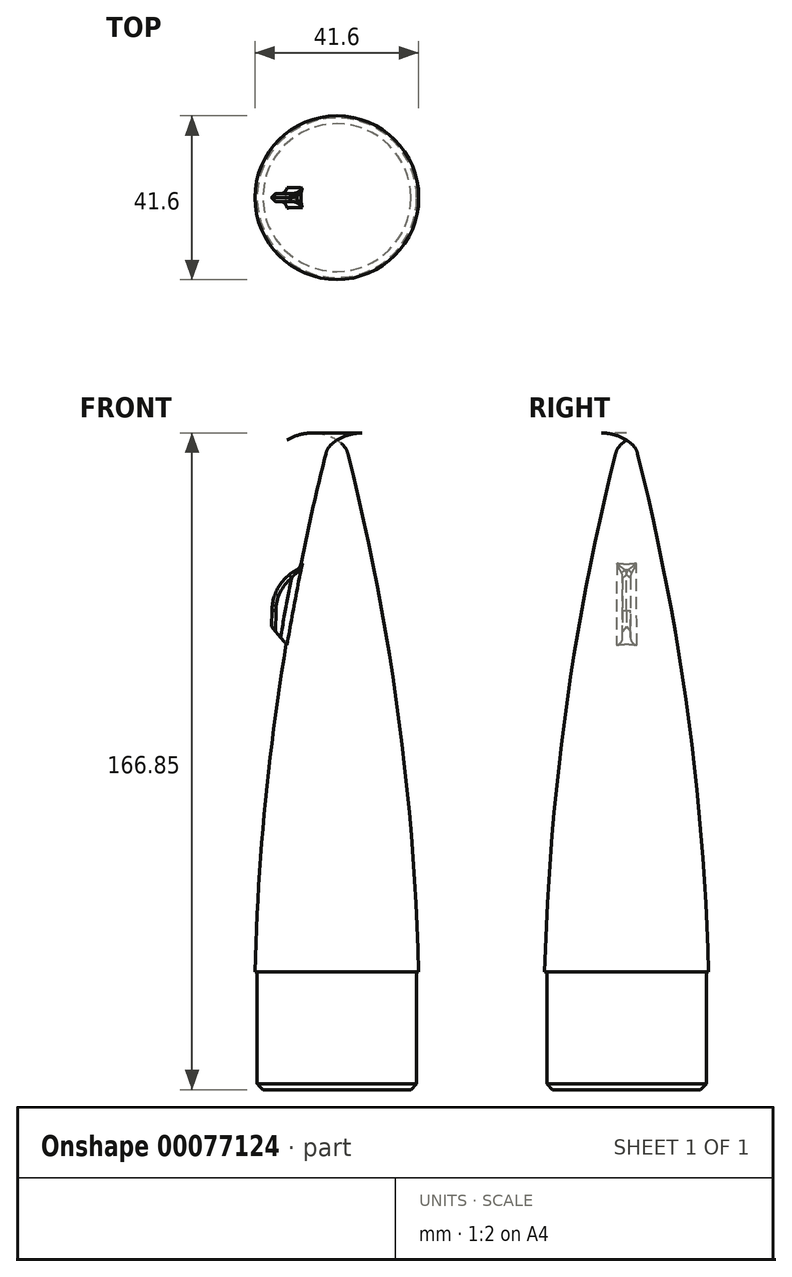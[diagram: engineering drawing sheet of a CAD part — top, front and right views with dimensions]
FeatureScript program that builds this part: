
annotation { "Feature Type Name" : "Feature", "Feature Type Description" : "" }
export const myFeature = defineFeature(function(context is Context, id is Id, definition is map)
    precondition{}
    {
        {
            var Q0;
            Q0=qCreatedBy(makeId("Front.planeOp"),FACE);
            var sketch = newSketch(context, id + "F0", { "sketchPlane" : qUnion([Q0])});
            skLineSegment(sketch, "E0", {"start": v(-20.8, -68.75) * mm, "end": v(-20.28, -68.75) * mm});
            skLineSegment(sketch, "E1", {"start": v(0, -68.75) * mm, "end": v(0, 86.96) * mm});
            skLineSegment(sketch, "E2", {"start": v(0, -68.75) * mm, "end": v(0, -98.75) * mm});
            skLineSegment(sketch, "E3", {"start": v(0, -98.75) * mm, "end": v(-20.28, -98.75) * mm});
            skLineSegment(sketch, "E4", {"start": v(-20.28, -98.75) * mm, "end": v(-20.28, -68.75) * mm});
            skLineSegment(sketch, "E5.trimOffspring", {"start": v(-20.28, -68.75) * mm, "end": v(-20.8, -68.75) * mm});
            skPoint(sketch, "E6.orphan", {"position": v(0, 71.25) * mm});
            skArc(sketch, "E7", {"start": v(0, 66.26) * mm, "mid": v(-1.3, 65.31) * mm, "end": v(-2.44, 64.2) * mm});
            skArc(sketch, "E8", {"start": v(-2.44, 64.2) * mm, "mid": v(-15.35, -1.76) * mm, "end": v(-20.8, -68.75) * mm});
            skPoint(sketch, "E8.second.point", {"position": v(1180, -68.75) * mm});
            skPoint(sketch, "E8.third.point", {"position": v(327.78, -629.15) * mm});
            skSolve(sketch);
        }
        {
            var Q0;
            Q0=makeQuery(id+"F0.imprint","IMPRINT",FACE,{"disambiguationData":[TD([[makeQuery(id+"F0.imprint","IMPRINT",EDGE,{"derivedFrom":sQuery(id+"F0.wireOp",EDGE,"Oh61cgLR-RQo2-T4aV-TcRg-Gp7ijPdUG9jl")}),1.0]])]});
            var Q1;
            {var subQ0=sQuery(id+"F0.wireOp",EDGE,"E2");Q1=makeQuery(id+"F0.imprint","IMPRINT",FACE,{"disambiguationData":[TD([[makeQuery(id+"F0.imprint","IMPRINT",EDGE,{"derivedFrom":subQ0}),-1.0]])]});}
            var Q2;
            Q2=sQuery(id+"F0.wireOp",EDGE,"E1");
            revolve(context, id + "F1", {"surfaceOperationType" : NewSurfaceOperationType.NEW, "entities" : qUnion([Q0, Q1]), "axis" : qUnion([Q2]), "revolveType" : RevolveType.FULL});
        }
        {
            var Q0;
            Q0=makeQuery(id+"F1.opRevolve","SWEPT_EDGE",EDGE,{"disambiguationData":[OSD([sQuery(id+"F0.wireOp",EDGE,"E3"),sQuery(id+"F0.wireOp",EDGE,"E4")])]});
            chamfer(context, id + "F2", {"entities" : qUnion([Q0]), "width" : 1.5 * mm, "tangentPropagation" : true});
        }
        {
            var Q0;
            Q0=qCreatedBy(makeId("Front.planeOp"),FACE);
            cPlane(context, id + "F3", {"entities" : qUnion([Q0]), "cplaneType" : CPlaneType.OFFSET, "offset" : 40 * mm, "width" : 150 * mm, "height" : 150 * mm});
        }
        {
            var Q0;
            Q0=qCreatedBy(id+"F3.planeOp",FACE);
            var sketch = newSketch(context, id + "F4", { "sketchPlane" : qUnion([Q0])});
            skText(sketch, "E9", { "text": "DC3Dparts", "fontName": "OpenSans-Regular.ttf"});
            const initialGuessF4  = {"E9": [-0.02787, -0.08817, 1, 0, 0.008]};
            skSetInitialGuess(sketch, initialGuessF4);
            skSolve(sketch);
        }
        {
            var Q0;
            Q0=qSketchRegion(id+"F4",true);
            var Q1;
            Q1=qCreatedBy(makeId("Front.planeOp"),FACE);
            extrude(context, id + "F5", {"entities" : qUnion([Q0]), "endBound" : BoundingType.UP_TO_SURFACE, "oppositeDirection" : true, "depth" : 25 * mm, "endBoundEntityFace" : qUnion([Q1]), "offsetDistance" : 25 * mm});
        }
        {
            var Q0;
            Q0=qCreatedBy(makeId("Front.planeOp"),FACE);
            var sketch = newSketch(context, id + "F6", { "sketchPlane" : qUnion([Q0])});
            skLineSegment(sketch, "E10.bottom", {"start": v(0, -71.45) * mm, "end": v(-32, -71.45) * mm});
            skLineSegment(sketch, "E10.top", {"start": v(0, -104.07) * mm, "end": v(-32, -104.07) * mm});
            skLineSegment(sketch, "E10.left", {"start": v(0, -71.45) * mm, "end": v(0, -104.07) * mm});
            skLineSegment(sketch, "E10.right", {"start": v(-32, -71.45) * mm, "end": v(-32, -104.07) * mm});
            skSolve(sketch);
        }
        {
            var Q0;
            Q0=makeQuery(id+"F6.imprint","IMPRINT",FACE,{"disambiguationData":[TD([[makeQuery(id+"F6.imprint","IMPRINT",EDGE,{"derivedFrom":sQuery(id+"F6.wireOp",EDGE,"E10.bottom")}),1.0]])]});
            var Q1;
            Q1=sQuery(id+"F6.wireOp",EDGE,"E10.left");
            revolve(context, id + "F7", {"entities" : qUnion([Q0]), "axis" : qUnion([Q1]), "revolveType" : RevolveType.FULL});
        }
        {
            var Q0;
            Q0=makeQuery(id+"F7.opRevolve","SWEPT_BODY",BODY,{"disambiguationData":[OSD([sQuery(id+"F6.wireOp",EDGE,"E10.bottom"),sQuery(id+"F6.wireOp",EDGE,"E10.top"),sQuery(id+"F6.wireOp",EDGE,"E10.left"),sQuery(id+"F6.wireOp",EDGE,"E10.right")])]});
            var Q1;
            Q1=makeQuery(id+"F5.opExtrude","SWEPT_BODY",BODY,{"disambiguationData":[OSD([sQuery(id+"F4.wireOp",EDGE,"E9.sketch_text.stroke-0"),sQuery(id+"F4.wireOp",EDGE,"E9.sketch_text.stroke-1"),sQuery(id+"F4.wireOp",EDGE,"E9.sketch_text.stroke-2"),sQuery(id+"F4.wireOp",EDGE,"E9.sketch_text.stroke-3"),sQuery(id+"F4.wireOp",EDGE,"E9.sketch_text.stroke-4"),sQuery(id+"F4.wireOp",EDGE,"E9.sketch_text.stroke-5"),sQuery(id+"F4.wireOp",EDGE,"E9.sketch_text.stroke-6"),sQuery(id+"F4.wireOp",EDGE,"E9.sketch_text.stroke-7"),sQuery(id+"F4.wireOp",EDGE,"E9.sketch_text.stroke-8"),sQuery(id+"F4.wireOp",EDGE,"E9.sketch_text.stroke-9"),sQuery(id+"F4.wireOp",EDGE,"E9.sketch_text.stroke-10"),sQuery(id+"F4.wireOp",EDGE,"E9.sketch_text.stroke-11"),sQuery(id+"F4.wireOp",EDGE,"E9.sketch_text.stroke-12"),sQuery(id+"F4.wireOp",EDGE,"E9.sketch_text.stroke-13")])]});
            var Q2;
            Q2=makeQuery(id+"F5.opExtrude","SWEPT_BODY",BODY,{"disambiguationData":[OSD([sQuery(id+"F4.wireOp",EDGE,"E9.sketch_text.stroke-14"),sQuery(id+"F4.wireOp",EDGE,"E9.sketch_text.stroke-15"),sQuery(id+"F4.wireOp",EDGE,"E9.sketch_text.stroke-16"),sQuery(id+"F4.wireOp",EDGE,"E9.sketch_text.stroke-17"),sQuery(id+"F4.wireOp",EDGE,"E9.sketch_text.stroke-18"),sQuery(id+"F4.wireOp",EDGE,"E9.sketch_text.stroke-19"),sQuery(id+"F4.wireOp",EDGE,"E9.sketch_text.stroke-20"),sQuery(id+"F4.wireOp",EDGE,"E9.sketch_text.stroke-21"),sQuery(id+"F4.wireOp",EDGE,"E9.sketch_text.stroke-22"),sQuery(id+"F4.wireOp",EDGE,"E9.sketch_text.stroke-23"),sQuery(id+"F4.wireOp",EDGE,"E9.sketch_text.stroke-24"),sQuery(id+"F4.wireOp",EDGE,"E9.sketch_text.stroke-25"),sQuery(id+"F4.wireOp",EDGE,"E9.sketch_text.stroke-26"),sQuery(id+"F4.wireOp",EDGE,"E9.sketch_text.stroke-27"),sQuery(id+"F4.wireOp",EDGE,"E9.sketch_text.stroke-28")])]});
            var Q3;
            Q3=makeQuery(id+"F5.opExtrude","SWEPT_BODY",BODY,{"disambiguationData":[OSD([sQuery(id+"F4.wireOp",EDGE,"E9.sketch_text.stroke-29"),sQuery(id+"F4.wireOp",EDGE,"E9.sketch_text.stroke-30"),sQuery(id+"F4.wireOp",EDGE,"E9.sketch_text.stroke-31"),sQuery(id+"F4.wireOp",EDGE,"E9.sketch_text.stroke-32"),sQuery(id+"F4.wireOp",EDGE,"E9.sketch_text.stroke-33"),sQuery(id+"F4.wireOp",EDGE,"E9.sketch_text.stroke-34"),sQuery(id+"F4.wireOp",EDGE,"E9.sketch_text.stroke-35"),sQuery(id+"F4.wireOp",EDGE,"E9.sketch_text.stroke-36"),sQuery(id+"F4.wireOp",EDGE,"E9.sketch_text.stroke-37"),sQuery(id+"F4.wireOp",EDGE,"E9.sketch_text.stroke-38"),sQuery(id+"F4.wireOp",EDGE,"E9.sketch_text.stroke-39"),sQuery(id+"F4.wireOp",EDGE,"E9.sketch_text.stroke-40"),sQuery(id+"F4.wireOp",EDGE,"E9.sketch_text.stroke-41"),sQuery(id+"F4.wireOp",EDGE,"E9.sketch_text.stroke-42"),sQuery(id+"F4.wireOp",EDGE,"E9.sketch_text.stroke-43"),sQuery(id+"F4.wireOp",EDGE,"E9.sketch_text.stroke-44"),sQuery(id+"F4.wireOp",EDGE,"E9.sketch_text.stroke-45"),sQuery(id+"F4.wireOp",EDGE,"E9.sketch_text.stroke-46"),sQuery(id+"F4.wireOp",EDGE,"E9.sketch_text.stroke-47"),sQuery(id+"F4.wireOp",EDGE,"E9.sketch_text.stroke-48"),sQuery(id+"F4.wireOp",EDGE,"E9.sketch_text.stroke-49"),sQuery(id+"F4.wireOp",EDGE,"E9.sketch_text.stroke-50"),sQuery(id+"F4.wireOp",EDGE,"E9.sketch_text.stroke-51"),sQuery(id+"F4.wireOp",EDGE,"E9.sketch_text.stroke-52"),sQuery(id+"F4.wireOp",EDGE,"E9.sketch_text.stroke-53"),sQuery(id+"F4.wireOp",EDGE,"E9.sketch_text.stroke-54"),sQuery(id+"F4.wireOp",EDGE,"E9.sketch_text.stroke-55"),sQuery(id+"F4.wireOp",EDGE,"E9.sketch_text.stroke-56")])]});
            var Q4;
            Q4=makeQuery(id+"F5.opExtrude","SWEPT_BODY",BODY,{"disambiguationData":[OSD([sQuery(id+"F4.wireOp",EDGE,"E9.sketch_text.stroke-57"),sQuery(id+"F4.wireOp",EDGE,"E9.sketch_text.stroke-58"),sQuery(id+"F4.wireOp",EDGE,"E9.sketch_text.stroke-59"),sQuery(id+"F4.wireOp",EDGE,"E9.sketch_text.stroke-60"),sQuery(id+"F4.wireOp",EDGE,"E9.sketch_text.stroke-61"),sQuery(id+"F4.wireOp",EDGE,"E9.sketch_text.stroke-62"),sQuery(id+"F4.wireOp",EDGE,"E9.sketch_text.stroke-63"),sQuery(id+"F4.wireOp",EDGE,"E9.sketch_text.stroke-64"),sQuery(id+"F4.wireOp",EDGE,"E9.sketch_text.stroke-65"),sQuery(id+"F4.wireOp",EDGE,"E9.sketch_text.stroke-66"),sQuery(id+"F4.wireOp",EDGE,"E9.sketch_text.stroke-67"),sQuery(id+"F4.wireOp",EDGE,"E9.sketch_text.stroke-68"),sQuery(id+"F4.wireOp",EDGE,"E9.sketch_text.stroke-69"),sQuery(id+"F4.wireOp",EDGE,"E9.sketch_text.stroke-70")])]});
            var Q5;
            Q5=makeQuery(id+"F5.opExtrude","SWEPT_BODY",BODY,{"disambiguationData":[OSD([sQuery(id+"F4.wireOp",EDGE,"E9.sketch_text.stroke-71"),sQuery(id+"F4.wireOp",EDGE,"E9.sketch_text.stroke-72"),sQuery(id+"F4.wireOp",EDGE,"E9.sketch_text.stroke-73"),sQuery(id+"F4.wireOp",EDGE,"E9.sketch_text.stroke-74"),sQuery(id+"F4.wireOp",EDGE,"E9.sketch_text.stroke-75"),sQuery(id+"F4.wireOp",EDGE,"E9.sketch_text.stroke-76"),sQuery(id+"F4.wireOp",EDGE,"E9.sketch_text.stroke-77"),sQuery(id+"F4.wireOp",EDGE,"E9.sketch_text.stroke-78"),sQuery(id+"F4.wireOp",EDGE,"E9.sketch_text.stroke-79"),sQuery(id+"F4.wireOp",EDGE,"E9.sketch_text.stroke-80"),sQuery(id+"F4.wireOp",EDGE,"E9.sketch_text.stroke-81"),sQuery(id+"F4.wireOp",EDGE,"E9.sketch_text.stroke-82"),sQuery(id+"F4.wireOp",EDGE,"E9.sketch_text.stroke-83"),sQuery(id+"F4.wireOp",EDGE,"E9.sketch_text.stroke-84"),sQuery(id+"F4.wireOp",EDGE,"E9.sketch_text.stroke-85"),sQuery(id+"F4.wireOp",EDGE,"E9.sketch_text.stroke-86"),sQuery(id+"F4.wireOp",EDGE,"E9.sketch_text.stroke-87"),sQuery(id+"F4.wireOp",EDGE,"E9.sketch_text.stroke-88"),sQuery(id+"F4.wireOp",EDGE,"E9.sketch_text.stroke-89"),sQuery(id+"F4.wireOp",EDGE,"E9.sketch_text.stroke-90"),sQuery(id+"F4.wireOp",EDGE,"E9.sketch_text.stroke-91"),sQuery(id+"F4.wireOp",EDGE,"E9.sketch_text.stroke-92"),sQuery(id+"F4.wireOp",EDGE,"E9.sketch_text.stroke-93"),sQuery(id+"F4.wireOp",EDGE,"E9.sketch_text.stroke-94"),sQuery(id+"F4.wireOp",EDGE,"E9.sketch_text.stroke-95")])]});
            var Q6;
            Q6=makeQuery(id+"F5.opExtrude","SWEPT_BODY",BODY,{"disambiguationData":[OSD([sQuery(id+"F4.wireOp",EDGE,"E9.sketch_text.stroke-136"),sQuery(id+"F4.wireOp",EDGE,"E9.sketch_text.stroke-137"),sQuery(id+"F4.wireOp",EDGE,"E9.sketch_text.stroke-138"),sQuery(id+"F4.wireOp",EDGE,"E9.sketch_text.stroke-139"),sQuery(id+"F4.wireOp",EDGE,"E9.sketch_text.stroke-140"),sQuery(id+"F4.wireOp",EDGE,"E9.sketch_text.stroke-141"),sQuery(id+"F4.wireOp",EDGE,"E9.sketch_text.stroke-142"),sQuery(id+"F4.wireOp",EDGE,"E9.sketch_text.stroke-143"),sQuery(id+"F4.wireOp",EDGE,"E9.sketch_text.stroke-144"),sQuery(id+"F4.wireOp",EDGE,"E9.sketch_text.stroke-145"),sQuery(id+"F4.wireOp",EDGE,"E9.sketch_text.stroke-146"),sQuery(id+"F4.wireOp",EDGE,"E9.sketch_text.stroke-147"),sQuery(id+"F4.wireOp",EDGE,"E9.sketch_text.stroke-148"),sQuery(id+"F4.wireOp",EDGE,"E9.sketch_text.stroke-149"),sQuery(id+"F4.wireOp",EDGE,"E9.sketch_text.stroke-150"),sQuery(id+"F4.wireOp",EDGE,"E9.sketch_text.stroke-151"),sQuery(id+"F4.wireOp",EDGE,"E9.sketch_text.stroke-152"),sQuery(id+"F4.wireOp",EDGE,"E9.sketch_text.stroke-153"),sQuery(id+"F4.wireOp",EDGE,"E9.sketch_text.stroke-154")])]});
            var Q7;
            Q7=makeQuery(id+"F5.opExtrude","SWEPT_BODY",BODY,{"disambiguationData":[OSD([sQuery(id+"F4.wireOp",EDGE,"E9.sketch_text.stroke-155"),sQuery(id+"F4.wireOp",EDGE,"E9.sketch_text.stroke-156"),sQuery(id+"F4.wireOp",EDGE,"E9.sketch_text.stroke-157"),sQuery(id+"F4.wireOp",EDGE,"E9.sketch_text.stroke-158"),sQuery(id+"F4.wireOp",EDGE,"E9.sketch_text.stroke-159"),sQuery(id+"F4.wireOp",EDGE,"E9.sketch_text.stroke-160"),sQuery(id+"F4.wireOp",EDGE,"E9.sketch_text.stroke-161"),sQuery(id+"F4.wireOp",EDGE,"E9.sketch_text.stroke-162"),sQuery(id+"F4.wireOp",EDGE,"E9.sketch_text.stroke-163"),sQuery(id+"F4.wireOp",EDGE,"E9.sketch_text.stroke-164"),sQuery(id+"F4.wireOp",EDGE,"E9.sketch_text.stroke-165"),sQuery(id+"F4.wireOp",EDGE,"E9.sketch_text.stroke-166"),sQuery(id+"F4.wireOp",EDGE,"E9.sketch_text.stroke-167"),sQuery(id+"F4.wireOp",EDGE,"E9.sketch_text.stroke-168"),sQuery(id+"F4.wireOp",EDGE,"E9.sketch_text.stroke-169"),sQuery(id+"F4.wireOp",EDGE,"E9.sketch_text.stroke-170"),sQuery(id+"F4.wireOp",EDGE,"E9.sketch_text.stroke-171"),sQuery(id+"F4.wireOp",EDGE,"E9.sketch_text.stroke-172"),sQuery(id+"F4.wireOp",EDGE,"E9.sketch_text.stroke-173"),sQuery(id+"F4.wireOp",EDGE,"E9.sketch_text.stroke-174"),sQuery(id+"F4.wireOp",EDGE,"E9.sketch_text.stroke-175"),sQuery(id+"F4.wireOp",EDGE,"E9.sketch_text.stroke-176"),sQuery(id+"F4.wireOp",EDGE,"E9.sketch_text.stroke-177"),sQuery(id+"F4.wireOp",EDGE,"E9.sketch_text.stroke-178"),sQuery(id+"F4.wireOp",EDGE,"E9.sketch_text.stroke-179")])]});
            var Q8;
            Q8=makeQuery(id+"F5.opExtrude","SWEPT_BODY",BODY,{"disambiguationData":[OSD([sQuery(id+"F4.wireOp",EDGE,"E9.sketch_text.stroke-96"),sQuery(id+"F4.wireOp",EDGE,"E9.sketch_text.stroke-97"),sQuery(id+"F4.wireOp",EDGE,"E9.sketch_text.stroke-98"),sQuery(id+"F4.wireOp",EDGE,"E9.sketch_text.stroke-99"),sQuery(id+"F4.wireOp",EDGE,"E9.sketch_text.stroke-100"),sQuery(id+"F4.wireOp",EDGE,"E9.sketch_text.stroke-101"),sQuery(id+"F4.wireOp",EDGE,"E9.sketch_text.stroke-102"),sQuery(id+"F4.wireOp",EDGE,"E9.sketch_text.stroke-103"),sQuery(id+"F4.wireOp",EDGE,"E9.sketch_text.stroke-104"),sQuery(id+"F4.wireOp",EDGE,"E9.sketch_text.stroke-105"),sQuery(id+"F4.wireOp",EDGE,"E9.sketch_text.stroke-106"),sQuery(id+"F4.wireOp",EDGE,"E9.sketch_text.stroke-107"),sQuery(id+"F4.wireOp",EDGE,"E9.sketch_text.stroke-108"),sQuery(id+"F4.wireOp",EDGE,"E9.sketch_text.stroke-109"),sQuery(id+"F4.wireOp",EDGE,"E9.sketch_text.stroke-110"),sQuery(id+"F4.wireOp",EDGE,"E9.sketch_text.stroke-111"),sQuery(id+"F4.wireOp",EDGE,"E9.sketch_text.stroke-112"),sQuery(id+"F4.wireOp",EDGE,"E9.sketch_text.stroke-113"),sQuery(id+"F4.wireOp",EDGE,"E9.sketch_text.stroke-114"),sQuery(id+"F4.wireOp",EDGE,"E9.sketch_text.stroke-115"),sQuery(id+"F4.wireOp",EDGE,"E9.sketch_text.stroke-116"),sQuery(id+"F4.wireOp",EDGE,"E9.sketch_text.stroke-117"),sQuery(id+"F4.wireOp",EDGE,"E9.sketch_text.stroke-118"),sQuery(id+"F4.wireOp",EDGE,"E9.sketch_text.stroke-119"),sQuery(id+"F4.wireOp",EDGE,"E9.sketch_text.stroke-120"),sQuery(id+"F4.wireOp",EDGE,"E9.sketch_text.stroke-121"),sQuery(id+"F4.wireOp",EDGE,"E9.sketch_text.stroke-122")])]});
            var Q9;
            Q9=makeQuery(id+"F5.opExtrude","SWEPT_BODY",BODY,{"disambiguationData":[OSD([sQuery(id+"F4.wireOp",EDGE,"E9.sketch_text.stroke-123"),sQuery(id+"F4.wireOp",EDGE,"E9.sketch_text.stroke-124"),sQuery(id+"F4.wireOp",EDGE,"E9.sketch_text.stroke-125"),sQuery(id+"F4.wireOp",EDGE,"E9.sketch_text.stroke-126"),sQuery(id+"F4.wireOp",EDGE,"E9.sketch_text.stroke-127"),sQuery(id+"F4.wireOp",EDGE,"E9.sketch_text.stroke-128"),sQuery(id+"F4.wireOp",EDGE,"E9.sketch_text.stroke-129"),sQuery(id+"F4.wireOp",EDGE,"E9.sketch_text.stroke-130"),sQuery(id+"F4.wireOp",EDGE,"E9.sketch_text.stroke-131"),sQuery(id+"F4.wireOp",EDGE,"E9.sketch_text.stroke-132"),sQuery(id+"F4.wireOp",EDGE,"E9.sketch_text.stroke-133"),sQuery(id+"F4.wireOp",EDGE,"E9.sketch_text.stroke-134"),sQuery(id+"F4.wireOp",EDGE,"E9.sketch_text.stroke-135")])]});
            booleanBodies(context, id + "F8", {"operationType" : BooleanOperationType.SUBTRACTION, "tools" : qUnion([Q0]), "targets" : qUnion([Q1, Q2, Q3, Q4, Q5, Q6, Q7, Q8, Q9])});
        }
        {
            var Q0;
            Q0=makeQuery(id+"F5.opExtrude","SWEPT_BODY",BODY,{"disambiguationData":[OSD([sQuery(id+"F4.wireOp",EDGE,"E9.sketch_text.stroke-0"),sQuery(id+"F4.wireOp",EDGE,"E9.sketch_text.stroke-1"),sQuery(id+"F4.wireOp",EDGE,"E9.sketch_text.stroke-2"),sQuery(id+"F4.wireOp",EDGE,"E9.sketch_text.stroke-3"),sQuery(id+"F4.wireOp",EDGE,"E9.sketch_text.stroke-4"),sQuery(id+"F4.wireOp",EDGE,"E9.sketch_text.stroke-5"),sQuery(id+"F4.wireOp",EDGE,"E9.sketch_text.stroke-6"),sQuery(id+"F4.wireOp",EDGE,"E9.sketch_text.stroke-7"),sQuery(id+"F4.wireOp",EDGE,"E9.sketch_text.stroke-8"),sQuery(id+"F4.wireOp",EDGE,"E9.sketch_text.stroke-9"),sQuery(id+"F4.wireOp",EDGE,"E9.sketch_text.stroke-10"),sQuery(id+"F4.wireOp",EDGE,"E9.sketch_text.stroke-11"),sQuery(id+"F4.wireOp",EDGE,"E9.sketch_text.stroke-12"),sQuery(id+"F4.wireOp",EDGE,"E9.sketch_text.stroke-13")])]});
            var Q1;
            Q1=makeQuery(id+"F5.opExtrude","SWEPT_BODY",BODY,{"disambiguationData":[OSD([sQuery(id+"F4.wireOp",EDGE,"E9.sketch_text.stroke-14"),sQuery(id+"F4.wireOp",EDGE,"E9.sketch_text.stroke-15"),sQuery(id+"F4.wireOp",EDGE,"E9.sketch_text.stroke-16"),sQuery(id+"F4.wireOp",EDGE,"E9.sketch_text.stroke-17"),sQuery(id+"F4.wireOp",EDGE,"E9.sketch_text.stroke-18"),sQuery(id+"F4.wireOp",EDGE,"E9.sketch_text.stroke-19"),sQuery(id+"F4.wireOp",EDGE,"E9.sketch_text.stroke-20"),sQuery(id+"F4.wireOp",EDGE,"E9.sketch_text.stroke-21"),sQuery(id+"F4.wireOp",EDGE,"E9.sketch_text.stroke-22"),sQuery(id+"F4.wireOp",EDGE,"E9.sketch_text.stroke-23"),sQuery(id+"F4.wireOp",EDGE,"E9.sketch_text.stroke-24"),sQuery(id+"F4.wireOp",EDGE,"E9.sketch_text.stroke-25"),sQuery(id+"F4.wireOp",EDGE,"E9.sketch_text.stroke-26"),sQuery(id+"F4.wireOp",EDGE,"E9.sketch_text.stroke-27"),sQuery(id+"F4.wireOp",EDGE,"E9.sketch_text.stroke-28")])]});
            var Q2;
            Q2=makeQuery(id+"F5.opExtrude","SWEPT_BODY",BODY,{"disambiguationData":[OSD([sQuery(id+"F4.wireOp",EDGE,"E9.sketch_text.stroke-29"),sQuery(id+"F4.wireOp",EDGE,"E9.sketch_text.stroke-30"),sQuery(id+"F4.wireOp",EDGE,"E9.sketch_text.stroke-31"),sQuery(id+"F4.wireOp",EDGE,"E9.sketch_text.stroke-32"),sQuery(id+"F4.wireOp",EDGE,"E9.sketch_text.stroke-33"),sQuery(id+"F4.wireOp",EDGE,"E9.sketch_text.stroke-34"),sQuery(id+"F4.wireOp",EDGE,"E9.sketch_text.stroke-35"),sQuery(id+"F4.wireOp",EDGE,"E9.sketch_text.stroke-36"),sQuery(id+"F4.wireOp",EDGE,"E9.sketch_text.stroke-37"),sQuery(id+"F4.wireOp",EDGE,"E9.sketch_text.stroke-38"),sQuery(id+"F4.wireOp",EDGE,"E9.sketch_text.stroke-39"),sQuery(id+"F4.wireOp",EDGE,"E9.sketch_text.stroke-40"),sQuery(id+"F4.wireOp",EDGE,"E9.sketch_text.stroke-41"),sQuery(id+"F4.wireOp",EDGE,"E9.sketch_text.stroke-42"),sQuery(id+"F4.wireOp",EDGE,"E9.sketch_text.stroke-43"),sQuery(id+"F4.wireOp",EDGE,"E9.sketch_text.stroke-44"),sQuery(id+"F4.wireOp",EDGE,"E9.sketch_text.stroke-45"),sQuery(id+"F4.wireOp",EDGE,"E9.sketch_text.stroke-46"),sQuery(id+"F4.wireOp",EDGE,"E9.sketch_text.stroke-47"),sQuery(id+"F4.wireOp",EDGE,"E9.sketch_text.stroke-48"),sQuery(id+"F4.wireOp",EDGE,"E9.sketch_text.stroke-49"),sQuery(id+"F4.wireOp",EDGE,"E9.sketch_text.stroke-50"),sQuery(id+"F4.wireOp",EDGE,"E9.sketch_text.stroke-51"),sQuery(id+"F4.wireOp",EDGE,"E9.sketch_text.stroke-52"),sQuery(id+"F4.wireOp",EDGE,"E9.sketch_text.stroke-53"),sQuery(id+"F4.wireOp",EDGE,"E9.sketch_text.stroke-54"),sQuery(id+"F4.wireOp",EDGE,"E9.sketch_text.stroke-55"),sQuery(id+"F4.wireOp",EDGE,"E9.sketch_text.stroke-56")])]});
            var Q3;
            Q3=makeQuery(id+"F5.opExtrude","SWEPT_BODY",BODY,{"disambiguationData":[OSD([sQuery(id+"F4.wireOp",EDGE,"E9.sketch_text.stroke-57"),sQuery(id+"F4.wireOp",EDGE,"E9.sketch_text.stroke-58"),sQuery(id+"F4.wireOp",EDGE,"E9.sketch_text.stroke-59"),sQuery(id+"F4.wireOp",EDGE,"E9.sketch_text.stroke-60"),sQuery(id+"F4.wireOp",EDGE,"E9.sketch_text.stroke-61"),sQuery(id+"F4.wireOp",EDGE,"E9.sketch_text.stroke-62"),sQuery(id+"F4.wireOp",EDGE,"E9.sketch_text.stroke-63"),sQuery(id+"F4.wireOp",EDGE,"E9.sketch_text.stroke-64"),sQuery(id+"F4.wireOp",EDGE,"E9.sketch_text.stroke-65"),sQuery(id+"F4.wireOp",EDGE,"E9.sketch_text.stroke-66"),sQuery(id+"F4.wireOp",EDGE,"E9.sketch_text.stroke-67"),sQuery(id+"F4.wireOp",EDGE,"E9.sketch_text.stroke-68"),sQuery(id+"F4.wireOp",EDGE,"E9.sketch_text.stroke-69"),sQuery(id+"F4.wireOp",EDGE,"E9.sketch_text.stroke-70")])]});
            var Q4;
            Q4=makeQuery(id+"F5.opExtrude","SWEPT_BODY",BODY,{"disambiguationData":[OSD([sQuery(id+"F4.wireOp",EDGE,"E9.sketch_text.stroke-71"),sQuery(id+"F4.wireOp",EDGE,"E9.sketch_text.stroke-72"),sQuery(id+"F4.wireOp",EDGE,"E9.sketch_text.stroke-73"),sQuery(id+"F4.wireOp",EDGE,"E9.sketch_text.stroke-74"),sQuery(id+"F4.wireOp",EDGE,"E9.sketch_text.stroke-75"),sQuery(id+"F4.wireOp",EDGE,"E9.sketch_text.stroke-76"),sQuery(id+"F4.wireOp",EDGE,"E9.sketch_text.stroke-77"),sQuery(id+"F4.wireOp",EDGE,"E9.sketch_text.stroke-78"),sQuery(id+"F4.wireOp",EDGE,"E9.sketch_text.stroke-79"),sQuery(id+"F4.wireOp",EDGE,"E9.sketch_text.stroke-80"),sQuery(id+"F4.wireOp",EDGE,"E9.sketch_text.stroke-81"),sQuery(id+"F4.wireOp",EDGE,"E9.sketch_text.stroke-82"),sQuery(id+"F4.wireOp",EDGE,"E9.sketch_text.stroke-83"),sQuery(id+"F4.wireOp",EDGE,"E9.sketch_text.stroke-84"),sQuery(id+"F4.wireOp",EDGE,"E9.sketch_text.stroke-85"),sQuery(id+"F4.wireOp",EDGE,"E9.sketch_text.stroke-86"),sQuery(id+"F4.wireOp",EDGE,"E9.sketch_text.stroke-87"),sQuery(id+"F4.wireOp",EDGE,"E9.sketch_text.stroke-88"),sQuery(id+"F4.wireOp",EDGE,"E9.sketch_text.stroke-89"),sQuery(id+"F4.wireOp",EDGE,"E9.sketch_text.stroke-90"),sQuery(id+"F4.wireOp",EDGE,"E9.sketch_text.stroke-91"),sQuery(id+"F4.wireOp",EDGE,"E9.sketch_text.stroke-92"),sQuery(id+"F4.wireOp",EDGE,"E9.sketch_text.stroke-93"),sQuery(id+"F4.wireOp",EDGE,"E9.sketch_text.stroke-94"),sQuery(id+"F4.wireOp",EDGE,"E9.sketch_text.stroke-95")])]});
            var Q5;
            Q5=makeQuery(id+"F5.opExtrude","SWEPT_BODY",BODY,{"disambiguationData":[OSD([sQuery(id+"F4.wireOp",EDGE,"E9.sketch_text.stroke-96"),sQuery(id+"F4.wireOp",EDGE,"E9.sketch_text.stroke-97"),sQuery(id+"F4.wireOp",EDGE,"E9.sketch_text.stroke-98"),sQuery(id+"F4.wireOp",EDGE,"E9.sketch_text.stroke-99"),sQuery(id+"F4.wireOp",EDGE,"E9.sketch_text.stroke-100"),sQuery(id+"F4.wireOp",EDGE,"E9.sketch_text.stroke-101"),sQuery(id+"F4.wireOp",EDGE,"E9.sketch_text.stroke-102"),sQuery(id+"F4.wireOp",EDGE,"E9.sketch_text.stroke-103"),sQuery(id+"F4.wireOp",EDGE,"E9.sketch_text.stroke-104"),sQuery(id+"F4.wireOp",EDGE,"E9.sketch_text.stroke-105"),sQuery(id+"F4.wireOp",EDGE,"E9.sketch_text.stroke-106"),sQuery(id+"F4.wireOp",EDGE,"E9.sketch_text.stroke-107"),sQuery(id+"F4.wireOp",EDGE,"E9.sketch_text.stroke-108"),sQuery(id+"F4.wireOp",EDGE,"E9.sketch_text.stroke-109"),sQuery(id+"F4.wireOp",EDGE,"E9.sketch_text.stroke-110"),sQuery(id+"F4.wireOp",EDGE,"E9.sketch_text.stroke-111"),sQuery(id+"F4.wireOp",EDGE,"E9.sketch_text.stroke-112"),sQuery(id+"F4.wireOp",EDGE,"E9.sketch_text.stroke-113"),sQuery(id+"F4.wireOp",EDGE,"E9.sketch_text.stroke-114"),sQuery(id+"F4.wireOp",EDGE,"E9.sketch_text.stroke-115"),sQuery(id+"F4.wireOp",EDGE,"E9.sketch_text.stroke-116"),sQuery(id+"F4.wireOp",EDGE,"E9.sketch_text.stroke-117"),sQuery(id+"F4.wireOp",EDGE,"E9.sketch_text.stroke-118"),sQuery(id+"F4.wireOp",EDGE,"E9.sketch_text.stroke-119"),sQuery(id+"F4.wireOp",EDGE,"E9.sketch_text.stroke-120"),sQuery(id+"F4.wireOp",EDGE,"E9.sketch_text.stroke-121"),sQuery(id+"F4.wireOp",EDGE,"E9.sketch_text.stroke-122")])]});
            var Q6;
            Q6=makeQuery(id+"F5.opExtrude","SWEPT_BODY",BODY,{"disambiguationData":[OSD([sQuery(id+"F4.wireOp",EDGE,"E9.sketch_text.stroke-123"),sQuery(id+"F4.wireOp",EDGE,"E9.sketch_text.stroke-124"),sQuery(id+"F4.wireOp",EDGE,"E9.sketch_text.stroke-125"),sQuery(id+"F4.wireOp",EDGE,"E9.sketch_text.stroke-126"),sQuery(id+"F4.wireOp",EDGE,"E9.sketch_text.stroke-127"),sQuery(id+"F4.wireOp",EDGE,"E9.sketch_text.stroke-128"),sQuery(id+"F4.wireOp",EDGE,"E9.sketch_text.stroke-129"),sQuery(id+"F4.wireOp",EDGE,"E9.sketch_text.stroke-130"),sQuery(id+"F4.wireOp",EDGE,"E9.sketch_text.stroke-131"),sQuery(id+"F4.wireOp",EDGE,"E9.sketch_text.stroke-132"),sQuery(id+"F4.wireOp",EDGE,"E9.sketch_text.stroke-133"),sQuery(id+"F4.wireOp",EDGE,"E9.sketch_text.stroke-134"),sQuery(id+"F4.wireOp",EDGE,"E9.sketch_text.stroke-135")])]});
            var Q7;
            Q7=makeQuery(id+"F5.opExtrude","SWEPT_BODY",BODY,{"disambiguationData":[OSD([sQuery(id+"F4.wireOp",EDGE,"E9.sketch_text.stroke-155"),sQuery(id+"F4.wireOp",EDGE,"E9.sketch_text.stroke-156"),sQuery(id+"F4.wireOp",EDGE,"E9.sketch_text.stroke-157"),sQuery(id+"F4.wireOp",EDGE,"E9.sketch_text.stroke-158"),sQuery(id+"F4.wireOp",EDGE,"E9.sketch_text.stroke-159"),sQuery(id+"F4.wireOp",EDGE,"E9.sketch_text.stroke-160"),sQuery(id+"F4.wireOp",EDGE,"E9.sketch_text.stroke-161"),sQuery(id+"F4.wireOp",EDGE,"E9.sketch_text.stroke-162"),sQuery(id+"F4.wireOp",EDGE,"E9.sketch_text.stroke-163"),sQuery(id+"F4.wireOp",EDGE,"E9.sketch_text.stroke-164"),sQuery(id+"F4.wireOp",EDGE,"E9.sketch_text.stroke-165"),sQuery(id+"F4.wireOp",EDGE,"E9.sketch_text.stroke-166"),sQuery(id+"F4.wireOp",EDGE,"E9.sketch_text.stroke-167"),sQuery(id+"F4.wireOp",EDGE,"E9.sketch_text.stroke-168"),sQuery(id+"F4.wireOp",EDGE,"E9.sketch_text.stroke-169"),sQuery(id+"F4.wireOp",EDGE,"E9.sketch_text.stroke-170"),sQuery(id+"F4.wireOp",EDGE,"E9.sketch_text.stroke-171"),sQuery(id+"F4.wireOp",EDGE,"E9.sketch_text.stroke-172"),sQuery(id+"F4.wireOp",EDGE,"E9.sketch_text.stroke-173"),sQuery(id+"F4.wireOp",EDGE,"E9.sketch_text.stroke-174"),sQuery(id+"F4.wireOp",EDGE,"E9.sketch_text.stroke-175"),sQuery(id+"F4.wireOp",EDGE,"E9.sketch_text.stroke-176"),sQuery(id+"F4.wireOp",EDGE,"E9.sketch_text.stroke-177"),sQuery(id+"F4.wireOp",EDGE,"E9.sketch_text.stroke-178"),sQuery(id+"F4.wireOp",EDGE,"E9.sketch_text.stroke-179")])]});
            var Q8;
            Q8=makeQuery(id+"F5.opExtrude","SWEPT_BODY",BODY,{"disambiguationData":[OSD([sQuery(id+"F4.wireOp",EDGE,"E9.sketch_text.stroke-136"),sQuery(id+"F4.wireOp",EDGE,"E9.sketch_text.stroke-137"),sQuery(id+"F4.wireOp",EDGE,"E9.sketch_text.stroke-138"),sQuery(id+"F4.wireOp",EDGE,"E9.sketch_text.stroke-139"),sQuery(id+"F4.wireOp",EDGE,"E9.sketch_text.stroke-140"),sQuery(id+"F4.wireOp",EDGE,"E9.sketch_text.stroke-141"),sQuery(id+"F4.wireOp",EDGE,"E9.sketch_text.stroke-142"),sQuery(id+"F4.wireOp",EDGE,"E9.sketch_text.stroke-143"),sQuery(id+"F4.wireOp",EDGE,"E9.sketch_text.stroke-144"),sQuery(id+"F4.wireOp",EDGE,"E9.sketch_text.stroke-145"),sQuery(id+"F4.wireOp",EDGE,"E9.sketch_text.stroke-146"),sQuery(id+"F4.wireOp",EDGE,"E9.sketch_text.stroke-147"),sQuery(id+"F4.wireOp",EDGE,"E9.sketch_text.stroke-148"),sQuery(id+"F4.wireOp",EDGE,"E9.sketch_text.stroke-149"),sQuery(id+"F4.wireOp",EDGE,"E9.sketch_text.stroke-150"),sQuery(id+"F4.wireOp",EDGE,"E9.sketch_text.stroke-151"),sQuery(id+"F4.wireOp",EDGE,"E9.sketch_text.stroke-152"),sQuery(id+"F4.wireOp",EDGE,"E9.sketch_text.stroke-153"),sQuery(id+"F4.wireOp",EDGE,"E9.sketch_text.stroke-154")])]});
            var Q9;
            Q9=makeQuery(id+"F1.opRevolve","SWEPT_BODY",BODY,{"disambiguationData":[OSD([sQuery(id+"F0.wireOp",EDGE,"Oh61cgLR-RQo2-T4aV-TcRg-Gp7ijPdUG9jl"),sQuery(id+"F0.wireOp",EDGE,"E1"),sQuery(id+"F0.wireOp",EDGE,"E2"),sQuery(id+"F0.wireOp",EDGE,"E3"),sQuery(id+"F0.wireOp",EDGE,"E4"),sQuery(id+"F0.wireOp",EDGE,"E5.trimOffspring"),sQuery(id+"F0.wireOp",EDGE,"dTV1AxgJ-VMAe-DLQO-Zqz3-4UbtDb8FiUJC")])]});
            booleanBodies(context, id + "F9", {"operationType" : BooleanOperationType.SUBTRACTION, "tools" : qUnion([Q0, Q1, Q2, Q3, Q4, Q5, Q6, Q7, Q8]), "targets" : qUnion([Q9])});
        }
        {
            var Q0;
            Q0=makeQuery(id+"F1.opRevolve","SWEPT_EDGE",EDGE,{"disambiguationData":[OSD([sQuery(id+"F0.wireOp",EDGE,"E7"),sQuery(id+"F0.wireOp",EDGE,"E8")])]});
            fillet(context, id + "F10", {"entities" : qUnion([Q0]), "radius" : 5 * mm, "tangentPropagation" : true, "allowEdgeOverflow" : false});
        }
        {
            var Q0;
            Q0=qCreatedBy(makeId("Front.planeOp"),FACE);
            var sketch = newSketch(context, id + "F11", { "sketchPlane" : qUnion([Q0])});
            skArc(sketch, "E11", {"start": v(-8.7, 34.02) * mm, "mid": v(-14.33, 29.71) * mm, "end": v(-16.5, 22.97) * mm});
            skLineSegment(sketch, "E12", {"start": v(-8.7, 34.02) * mm, "end": v(-12.38, 13.85) * mm});
            skArc(sketch, "E13.MirrorCS", {"start": v(8.7, 34.02) * mm, "mid": v(14.33, 29.71) * mm, "end": v(16.5, 22.97) * mm});
            skLineSegment(sketch, "E14.MirrorCS", {"start": v(8.7, 34.02) * mm, "end": v(12.38, 13.85) * mm});
            skLineSegment(sketch, "E15", {"start": v(-12.38, 13.85) * mm, "end": v(-16.6, 18.9) * mm});
            skLineSegment(sketch, "E16", {"start": v(-16.6, 18.9) * mm, "end": v(-16.5, 22.97) * mm});
            skLineSegment(sketch, "E17.MirrorCS", {"start": v(12.38, 13.85) * mm, "end": v(16.6, 18.9) * mm});
            skLineSegment(sketch, "E18.MirrorCS", {"start": v(16.6, 18.9) * mm, "end": v(16.5, 22.97) * mm});
            skPoint(sketch, "E19.orphan", {"position": v(12.38, 13.85) * mm});
            skSolve(sketch);
        }
        {
            var Q0;
            Q0=makeQuery(id+"F11.imprint","IMPRINT",FACE,{"disambiguationData":[TD([[makeQuery(id+"F11.imprint","IMPRINT",EDGE,{"derivedFrom":sQuery(id+"F11.wireOp",EDGE,"E11")}),1.0]])]});
            var Q1;
            Q1=makeQuery(id+"F11.imprint","IMPRINT",FACE,{"disambiguationData":[TD([[makeQuery(id+"F11.imprint","IMPRINT",EDGE,{"derivedFrom":sQuery(id+"F11.wireOp",EDGE,"E13.MirrorCS")}),-1.0]])]});
            extrude(context, id + "F12", {"entities" : qUnion([Q0, Q1]), "operationType" : NewBodyOperationType.ADD, "depth" : 2 * mm, "offsetDistance" : 25 * mm, "symmetric" : true});
        }
        {
            var Q0;
            Q0=makeQuery(id+"F12.boolean.opBoolean","INTERSECT",EDGE,{"derivedFrom":[makeQuery(id+"F1.opRevolve","SWEPT_FACE",FACE,{"disambiguationData":[OSD([sQuery(id+"F0.wireOp",EDGE,"E8")])]}),makeQuery(id+"F12.opExtrude","CAP_FACE",FACE,{"disambiguationData":[OSD([sQuery(id+"F11.wireOp",EDGE,"E11"),sQuery(id+"F11.wireOp",EDGE,"E12")])],"isStart":false})]});
            var Q1;
            Q1=makeQuery(id+"F12.boolean.opBoolean","INTERSECT",EDGE,{"derivedFrom":[makeQuery(id+"F1.opRevolve","SWEPT_FACE",FACE,{"disambiguationData":[OSD([sQuery(id+"F0.wireOp",EDGE,"E8")])]}),makeQuery(id+"F12.opExtrude","CAP_FACE",FACE,{"disambiguationData":[OSD([sQuery(id+"F11.wireOp",EDGE,"E11"),sQuery(id+"F11.wireOp",EDGE,"E12")])],"isStart":true})]});
            var Q2;
            Q2=makeQuery(id+"F12.boolean.opBoolean","INTERSECT",EDGE,{"derivedFrom":[makeQuery(id+"F1.opRevolve","SWEPT_FACE",FACE,{"disambiguationData":[OSD([sQuery(id+"F0.wireOp",EDGE,"E8")])]}),makeQuery(id+"F12.opExtrude","CAP_FACE",FACE,{"disambiguationData":[OSD([sQuery(id+"F11.wireOp",EDGE,"E13.MirrorCS"),sQuery(id+"F11.wireOp",EDGE,"E14.MirrorCS")])],"isStart":true})]});
            var Q3;
            Q3=makeQuery(id+"F12.boolean.opBoolean","INTERSECT",EDGE,{"derivedFrom":[makeQuery(id+"F1.opRevolve","SWEPT_FACE",FACE,{"disambiguationData":[OSD([sQuery(id+"F0.wireOp",EDGE,"E8")])]}),makeQuery(id+"F12.opExtrude","CAP_FACE",FACE,{"disambiguationData":[OSD([sQuery(id+"F11.wireOp",EDGE,"E13.MirrorCS"),sQuery(id+"F11.wireOp",EDGE,"E14.MirrorCS")])],"isStart":false})]});
            var Q4;
            Q4=makeQuery(id+"F12.boolean.opBoolean","INTERSECT",EDGE,{"disambiguationData":[OD(0.0)],"derivedFrom":[makeQuery(id+"F1.opRevolve","SWEPT_FACE",FACE,{"disambiguationData":[OSD([sQuery(id+"F0.wireOp",EDGE,"E8")])]}),makeQuery(id+"F12.opExtrude","SWEPT_FACE",FACE,{"disambiguationData":[OSD([sQuery(id+"F11.wireOp",EDGE,"E13.MirrorCS")])]})]});
            var Q5;
            Q5=makeQuery(id+"F12.boolean.opBoolean","INTERSECT",EDGE,{"disambiguationData":[OD(1.0)],"derivedFrom":[makeQuery(id+"F1.opRevolve","SWEPT_FACE",FACE,{"disambiguationData":[OSD([sQuery(id+"F0.wireOp",EDGE,"E8")])]}),makeQuery(id+"F12.opExtrude","SWEPT_FACE",FACE,{"disambiguationData":[OSD([sQuery(id+"F11.wireOp",EDGE,"E13.MirrorCS")])]})]});
            var Q6;
            Q6=makeQuery(id+"F12.boolean.opBoolean","INTERSECT",EDGE,{"disambiguationData":[OD(1.0)],"derivedFrom":[makeQuery(id+"F1.opRevolve","SWEPT_FACE",FACE,{"disambiguationData":[OSD([sQuery(id+"F0.wireOp",EDGE,"E8")])]}),makeQuery(id+"F12.opExtrude","SWEPT_FACE",FACE,{"disambiguationData":[OSD([sQuery(id+"F11.wireOp",EDGE,"E11")])]})]});
            var Q7;
            Q7=makeQuery(id+"F12.boolean.opBoolean","INTERSECT",EDGE,{"disambiguationData":[OD(0.0)],"derivedFrom":[makeQuery(id+"F1.opRevolve","SWEPT_FACE",FACE,{"disambiguationData":[OSD([sQuery(id+"F0.wireOp",EDGE,"E8")])]}),makeQuery(id+"F12.opExtrude","SWEPT_FACE",FACE,{"disambiguationData":[OSD([sQuery(id+"F11.wireOp",EDGE,"E11")])]})]});
            fillet(context, id + "F13", {"entities" : qUnion([Q0, Q1, Q2, Q3, Q4, Q5, Q6, Q7]), "radius" : 2 * mm, "tangentPropagation" : true, "allowEdgeOverflow" : false});
        }
        {
            var Q0;
            Q0=makeQuery(id+"F12.opExtrude","CAP_EDGE",EDGE,{"disambiguationData":[OSD([sQuery(id+"F11.wireOp",EDGE,"E13.MirrorCS")])],"isStart":false});
            var Q1;
            Q1=makeQuery(id+"F12.opExtrude","CAP_EDGE",EDGE,{"disambiguationData":[OSD([sQuery(id+"F11.wireOp",EDGE,"E13.MirrorCS")])],"isStart":true});
            var Q2;
            Q2=makeQuery(id+"F12.opExtrude","CAP_EDGE",EDGE,{"disambiguationData":[OSD([sQuery(id+"F11.wireOp",EDGE,"E11")])],"isStart":false});
            var Q3;
            Q3=makeQuery(id+"F12.opExtrude","CAP_EDGE",EDGE,{"disambiguationData":[OSD([sQuery(id+"F11.wireOp",EDGE,"E11")])],"isStart":true});
            chamfer(context, id + "F14", {"entities" : qUnion([Q0, Q1, Q2, Q3]), "width" : 1 * mm, "tangentPropagation" : true});
        }
    });
